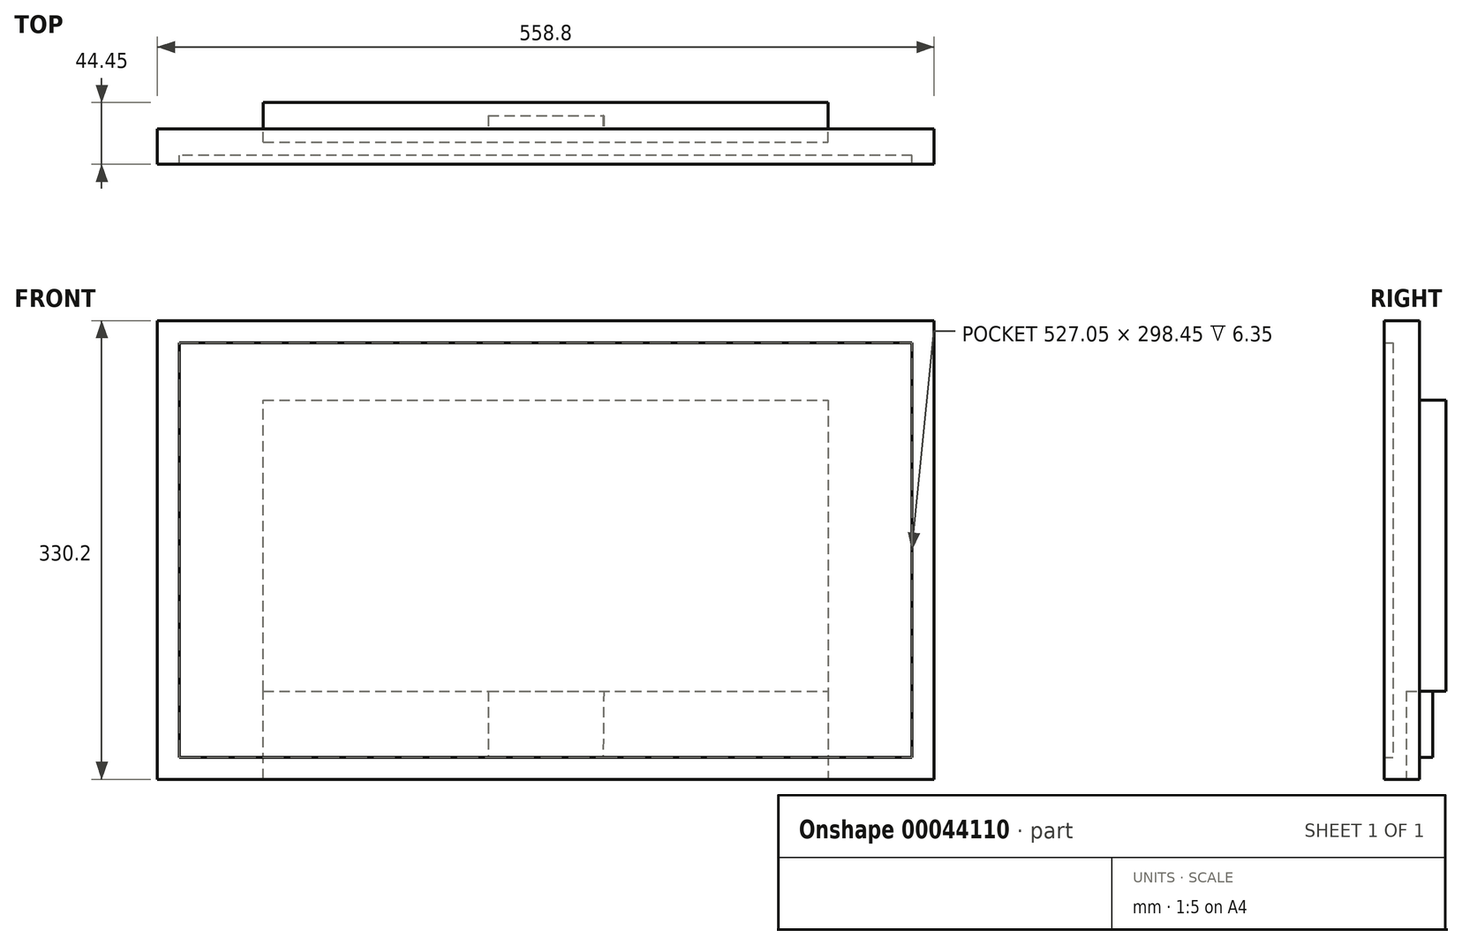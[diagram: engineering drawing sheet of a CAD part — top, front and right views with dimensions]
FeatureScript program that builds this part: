
annotation { "Feature Type Name" : "Feature", "Feature Type Description" : "" }
export const myFeature = defineFeature(function(context is Context, id is Id, definition is map)
    precondition{}
    {
        {
            var Q0;
            Q0=qCreatedBy(makeId("Front.planeOp"),FACE);
            var sketch = newSketch(context, id + "F0", { "sketchPlane" : qUnion([Q0])});
            skLineSegment(sketch, "E0.bottom", {"start": v(-289.1, 187.95) * mm, "end": v(269.7, 187.95) * mm});
            skLineSegment(sketch, "E0.top", {"start": v(-289.1, -142.25) * mm, "end": v(269.7, -142.25) * mm});
            skLineSegment(sketch, "E0.left", {"start": v(-289.1, 187.95) * mm, "end": v(-289.1, -142.25) * mm});
            skLineSegment(sketch, "E0.right", {"start": v(269.7, 187.95) * mm, "end": v(269.7, -142.25) * mm});
            skLineSegment(sketch, "E1", {"start": v(-273.23, 172.07) * mm, "end": v(-273.23, -126.38) * mm});
            skLineSegment(sketch, "E2", {"start": v(-273.23, -126.38) * mm, "end": v(253.82, -126.38) * mm});
            skLineSegment(sketch, "E3", {"start": v(253.82, -126.38) * mm, "end": v(253.82, 172.07) * mm});
            skLineSegment(sketch, "E4", {"start": v(253.82, 172.07) * mm, "end": v(-273.23, 172.07) * mm});
            skSolve(sketch);
        }
        {
            var Q0;
            Q0=makeQuery(id+"F0.imprint","IMPRINT",FACE,{"disambiguationData":[TD([[makeQuery(id+"F0.imprint","IMPRINT",EDGE,{"derivedFrom":sQuery(id+"F0.wireOp",EDGE,"E0.bottom")}),-1.0]])]});
            extrude(context, id + "F1", {"entities" : qUnion([Q0]), "depth" : 25.4 * mm});
        }
        {
            var Q0;
            Q0=makeQuery(id+"F0.imprint","IMPRINT",FACE,{"disambiguationData":[TD([[makeQuery(id+"F0.imprint","IMPRINT",EDGE,{"derivedFrom":sQuery(id+"F0.wireOp",EDGE,"E1")}),1.0]])]});
            extrude(context, id + "F2", {"entities" : qUnion([Q0]), "operationType" : NewBodyOperationType.ADD, "depth" : 19.05 * mm});
        }
        {
            var Q0;
            Q0=makeQuery(id+"F0.imprint","IMPRINT",FACE,{"disambiguationData":[TD([[makeQuery(id+"F0.imprint","IMPRINT",EDGE,{"derivedFrom":sQuery(id+"F0.wireOp",EDGE,"E1")}),1.0]])]});
            var sketch = newSketch(context, id + "F3", { "sketchPlane" : qUnion([Q0])});
            skLineSegment(sketch, "E5", {"start": v(-212.9, 130.8) * mm, "end": v(193.5, 130.8) * mm});
            skLineSegment(sketch, "E6", {"start": v(193.5, 130.8) * mm, "end": v(193.5, -78.75) * mm});
            skLineSegment(sketch, "E7", {"start": v(193.5, -78.75) * mm, "end": v(-212.9, -78.75) * mm});
            skLineSegment(sketch, "E8", {"start": v(-212.9, -78.75) * mm, "end": v(-212.9, 130.8) * mm});
            skSolve(sketch);
        }
        {
            var Q0;
            Q0=makeQuery(id+"F3.imprint","IMPRINT",FACE,{"disambiguationData":[TD([[makeQuery(id+"F3.imprint","IMPRINT",EDGE,{"derivedFrom":sQuery(id+"F3.wireOp",EDGE,"E5")}),-1.0]])]});
            extrude(context, id + "F4", {"entities" : qUnion([Q0]), "operationType" : NewBodyOperationType.ADD, "oppositeDirection" : true, "depth" : 19.05 * mm});
        }
        {
            var Q0;
            Q0=makeQuery(id+"F0.imprint","IMPRINT",FACE,{"disambiguationData":[TD([[makeQuery(id+"F0.imprint","IMPRINT",EDGE,{"derivedFrom":sQuery(id+"F0.wireOp",EDGE,"E1")}),1.0]])]});
            var sketch = newSketch(context, id + "F5", { "sketchPlane" : qUnion([Q0])});
            skPoint(sketch, "E9.0", {"position": v(193.5, -78.75) * mm});
            skPoint(sketch, "E10.0", {"position": v(-212.9, -78.75) * mm});
            skLineSegment(sketch, "E11", {"start": v(193.5, -78.75) * mm, "end": v(193.5, -142.25) * mm});
            skLineSegment(sketch, "E12", {"start": v(193.5, -142.25) * mm, "end": v(-212.9, -142.25) * mm});
            skLineSegment(sketch, "E13", {"start": v(-212.9, -142.25) * mm, "end": v(-212.9, -78.75) * mm});
            skLineSegment(sketch, "E14", {"start": v(-212.9, -78.75) * mm, "end": v(193.5, -78.75) * mm});
            skSolve(sketch);
        }
        {
            var Q0;
            {var subQ5=sQuery(id+"F5.wireOp",EDGE,"E12");Q0=makeQuery(id+"F5.imprint","IMPRINT",FACE,{"disambiguationData":[TD([[makeQuery(id+"F5.imprint","IMPRINT",EDGE,{"derivedFrom":subQ5}),-1.0]])]});}
            var Q1;
            {var subQ5=sQuery(id+"F5.wireOp",EDGE,"E14");Q1=makeQuery(id+"F5.imprint","IMPRINT",FACE,{"disambiguationData":[TD([[makeQuery(id+"F5.imprint","IMPRINT",EDGE,{"derivedFrom":subQ5}),-1.0]])]});}
            extrude(context, id + "F6", {"entities" : qUnion([Q0, Q1]), "operationType" : NewBodyOperationType.REMOVE, "depth" : 9.52 * mm});
        }
        {
            var Q0;
            {var subQ5=sQuery(id+"F5.wireOp",EDGE,"E14");Q0=makeQuery(id+"F5.imprint","IMPRINT",FACE,{"disambiguationData":[TD([[makeQuery(id+"F5.imprint","IMPRINT",EDGE,{"derivedFrom":subQ5}),-1.0]])]});}
            var sketch = newSketch(context, id + "F7", { "sketchPlane" : qUnion([Q0])});
            skLineSegment(sketch, "E15", {"start": v(31.57, -126.38) * mm, "end": v(-50.98, -126.38) * mm});
            skPoint(sketch, "E16.0", {"position": v(-212.9, -78.75) * mm});
            skLineSegment(sketch, "E17", {"start": v(-50.98, -78.75) * mm, "end": v(31.57, -78.75) * mm});
            skLineSegment(sketch, "E18", {"start": v(-50.98, -78.75) * mm, "end": v(-50.98, -126.38) * mm});
            skLineSegment(sketch, "E19", {"start": v(32, -78.67) * mm, "end": v(31.57, -126.38) * mm});
            skSolve(sketch);
        }
        {
            var Q0;
            {var subQ5=sQuery(id+"F7.wireOp",EDGE,"E15");Q0=makeQuery(id+"F7.imprint","IMPRINT",FACE,{"disambiguationData":[TD([[makeQuery(id+"F7.imprint","IMPRINT",EDGE,{"derivedFrom":subQ5}),1.0]])]});}
            extrude(context, id + "F8", {"entities" : qUnion([Q0]), "operationType" : NewBodyOperationType.ADD, "oppositeDirection" : true, "depth" : 9.52 * mm});
        }
    });
